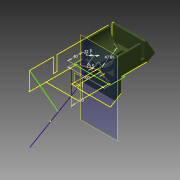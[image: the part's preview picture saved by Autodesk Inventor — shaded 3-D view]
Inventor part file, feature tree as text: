
AUTODESK INVENTOR PART (.ipt)
format: ipt  version: 2013 (Build 170138000, 138)  size: 357,888 bytes
history: native  units: mm
features: sketch x19, extrude x15, other x3
ambient origin geometry x8: Origin, YZ Plane, XZ Plane, XY Plane, X Axis, Y Axis, Z Axis, Center Point
feature tree (37):
  other  "ソリッド1"
  extrude  "押し出し1"  Depth=90.0mm
  extrude  "押し出し2"  Depth=50.0mm
  extrude  "押し出し3"  Depth=5.0mm
  extrude  "押し出し4"  Depth=85.0mm
  extrude  "押し出し6"  Depth=5.0mm
  sketch  "スケッチ9"
  extrude  "押し出し12"  Depth=80.0mm
  sketch  "スケッチ19"
  sketch  "スケッチ20"
  other  "作業平面5"
  extrude  "押し出し13"  Depth=10.0mm
  other  "作業平面6"
  extrude  "押し出し14"  Depth=90.0mm
  extrude  "押し出し15"  Depth=230.0mm TaperAngle=0.0deg
  sketch  "スケッチ24"
  sketch  "スケッチ25"
  extrude  "押し出し16"  Depth=225.0mm TaperAngle=0.0deg
  extrude  "押し出し17"  Depth=5.0mm TaperAngle=0.0deg
  extrude  "押し出し18"  Depth=65.0mm
  extrude  "押し出し19"  Depth=10.0mm
  extrude  "押し出し20"  Depth=140.0mm
  extrude  "押し出し21"  Depth=10.0mm
  sketch  "スケッチ1"
  sketch  "スケッチ2"
  sketch  "スケッチ3"
  sketch  "スケッチ4"
  sketch  "スケッチ6"
  sketch  "スケッチ18"
  sketch  "スケッチ21"
  sketch  "スケッチ22"
  sketch  "スケッチ23"
  sketch  "スケッチ26"
  sketch  "スケッチ27"
  sketch  "スケッチ28"
  sketch  "スケッチ29"
  sketch  "スケッチ30"
